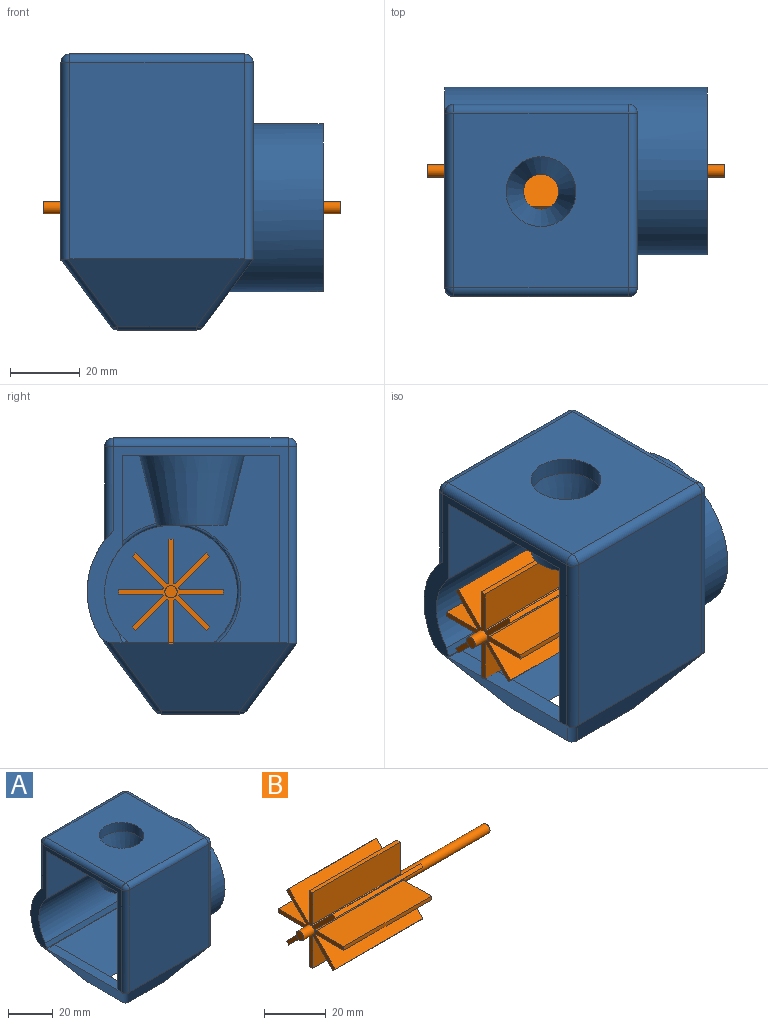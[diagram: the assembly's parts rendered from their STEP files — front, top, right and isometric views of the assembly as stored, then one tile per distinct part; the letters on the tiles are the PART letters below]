
ASSEMBLY  parts=2 mates=1
PART A: 60 faces, bbox 77.2x60.7x79.7 mm
  f0: cylinder r=19mm len=70mm, axis (-1,0,0), area 3704.2mm2, adj f1,f54,f55,f56,f57,f58,f59
  f1: plane 51.34x26.49mm, normal (0,-1,0), area 1308.1mm2, adj f0,f2,f53,f54,f58
  f2: plane 50x45mm, normal (0,0,-1), area 1543.1mm2, adj f1,f3,f52,f53,f54
  f3: plane 53.66x50mm, normal (0,1,0), area 2683.1mm2, adj f2,f4,f51,f53,f54
  f4: plane 45x5mm, normal (0,0,1), area 225mm2, adj f3,f5,f49,f50
  f5: plane 45x20.34mm, normal (0.8,0,0.59), area 758.1mm2, adj f4,f6,f48,f51
  f6: plane 22.48x22.48mm, normal (0,0,-1), area 280.1mm2, adj f5,f7,f9,f44,f45,f47,f48,f51
  f7: plane 45.1x20.58mm, normal (-0.8,0,0.59), area 653.9mm2, adj f6,f8,f48,f51,f53,f56,f57,f58
  f8: plane 0.44x0.42mm, normal (-1,0,0), area 0.1mm2, adj f7,f50,f55,f56
  f9: cylinder r=2.5mm len=22.48mm, axis (0,1,0), area 52.6mm2, adj f6,f10,f43,f49
  f10: sphere r=2.5mm, area 5.4mm2, adj f9,f11,f44
  f11: cylinder r=2.5mm len=19.59mm, axis (0.51,0.51,-0.69), area 84.3mm2, adj f10,f12,f42,f49
  f12: cylinder r=2.5mm len=56.22mm, axis (0,0,1), area 220.7mm2, adj f11,f13,f41,f42,f49,f54
  f13: sphere r=2.5mm, area 9.8mm2, adj f12,f14,f40
  f14: cylinder r=2.5mm len=50mm, axis (-1,0,0), area 196.3mm2, adj f13,f15,f39,f41
  f15: plane 50x50mm, normal (0,0,1), area 2185.8mm2, adj f14,f16,f19,f38,f40
  f16: cylinder r=10mm len=20mm, axis (0,0,-1), area 314.2mm2, adj f15,f17
  f17: cone r=10mm half-angle=14deg, axis (0,0,1), area 971.5mm2, adj f16,f18
  f18: plane 20x20mm, normal (0,0,-1), area 235.6mm2, adj f17,f52
  f19: cylinder r=2.5mm len=50mm, axis (1,0,0), area 196.3mm2, adj f15,f20,f36,f37
  f20: sphere r=2.5mm, area 9.8mm2, adj f19,f21,f40
  f21: cylinder r=2.5mm len=26.84mm, axis (0,0,1), area 100mm2, adj f20,f22,f36,f54
  f22: cylinder r=24mm len=75mm, axis (-1,0,0), area 4957.6mm2, adj f21,f23,f24,f26,f28,f32,f33,f34
  f23: cylinder r=24mm len=48mm, axis (-1,0,0), area 0mm2, adj f22,f35
  f24: plane 48x48mm, normal (1,0,0), area 1799.9mm2, adj f22,f25
  f25: cylinder r=1.75mm len=5mm, axis (-1,0,0), area 55mm2, adj f24,f59
  f26: cylinder r=2.5mm len=19.64mm, axis (-0.51,-0.51,-0.69), area 72.2mm2, adj f22,f27,f28,f35
  f27: sphere r=2.5mm, area 1.6mm2, adj f26,f45,f47
  f28: plane 46.83x19.35mm, normal (0.8,0,-0.59), area 583.5mm2, adj f22,f26,f29,f31,f32,f45
  f29: cylinder r=2.5mm len=19.59mm, axis (0.51,-0.51,0.69), area 84.3mm2, adj f28,f30,f31,f42
  f30: sphere r=2.5mm, area 4mm2, adj f29,f44,f45
  f31: cylinder r=2.5mm len=56.22mm, axis (0,0,-1), area 220.7mm2, adj f28,f29,f32,f39,f41,f42
  f32: plane 56.16x50mm, normal (1,0,0), area 1423.1mm2, adj f22,f28,f31,f33,f38
  f33: cylinder r=2.5mm len=26.84mm, axis (0,0,-1), area 100mm2, adj f22,f32,f36,f37
  f34: cylinder r=2.5mm len=21.73mm, axis (-0.51,0.51,0.69), area 89.3mm2, adj f22,f35,f43,f49,f54
  f35: plane 50.98x19.32mm, normal (0,0.8,-0.59), area 881.7mm2, adj f22,f23,f26,f34,f47
  f36: plane 50x26.84mm, normal (0,1,0), area 1341.9mm2, adj f19,f21,f22,f33
  f37: sphere r=2.5mm, area 6.2mm2, adj f19,f33,f38
  f38: cylinder r=2.5mm len=50mm, axis (0,-1,0), area 196.3mm2, adj f15,f32,f37,f39
  f39: sphere r=2.5mm, area 6.3mm2, adj f14,f31,f38
  f40: cylinder r=2.5mm len=50mm, axis (0,-1,0), area 196.3mm2, adj f13,f15,f20,f54
  f41: plane 56.16x50mm, normal (0,-1,0), area 2808.1mm2, adj f12,f14,f31,f42
  f42: plane 50.92x19.35mm, normal (0,-0.8,-0.59), area 881.7mm2, adj f11,f12,f29,f31,f41,f44
  f43: sphere r=2.5mm, area 5.4mm2, adj f9,f34,f47
  f44: cylinder r=2.5mm len=22.48mm, axis (1,0,0), area 52.6mm2, adj f6,f10,f30,f42
  f45: cylinder r=2.5mm len=22.48mm, axis (0,1,0), area 52.6mm2, adj f6,f27,f28,f30,f46
  f46: sphere r=2.5mm, area 0.4mm2, adj f45,f47
  f47: cylinder r=2.5mm len=22.48mm, axis (1,0,0), area 52.6mm2, adj f6,f27,f35,f43,f46
  f48: plane 45x20.34mm, normal (0,-0.8,0.59), area 758.1mm2, adj f5,f6,f7,f50
  f49: plane 50.96x19.35mm, normal (-0.8,0,-0.59), area 881.7mm2, adj f4,f9,f11,f12,f34,f54
  f50: plane 50x0.31mm, normal (0,-1,0), area 15.3mm2, adj f4,f8,f48,f54,f55
  f51: plane 45x20.34mm, normal (0,0.8,0.59), area 758.1mm2, adj f3,f5,f6,f7
  f52: cone r=15mm half-angle=14deg, axis (0,0,1), area 1619.1mm2, adj f2,f18
  f53: plane 53.66x45mm, normal (-1,0,0), area 1376mm2, adj f1,f2,f3,f7,f58
  f54: plane 58.17x56.83mm, normal (-1,0,0), area 480.4mm2, adj f0,f1,f2,f3,f12,f21,f22,f34
  f55: plane 51.46x3.01mm, normal (0,-0.94,0.33), area 135.8mm2, adj f0,f8,f50,f54,f56
  f56: torus R=20mm, axis (1,0,0), area 3.2mm2, adj f0,f7,f8,f55,f57
  f57: bspline ~26.48x5.21mm, area 29.1mm2, adj f0,f7,f56,f58
  f58: torus R=20mm, axis (1,0,0), area 97.7mm2, adj f0,f1,f7,f53,f57
  f59: plane 38x38mm, normal (-1,0,0), area 1124.5mm2, adj f0,f25
PART B: 38 faces, bbox 85x30x30 mm
  f0: cylinder r=15mm len=40mm, axis (-1,0,0), area 60mm2, adj f8,f9,f11,f32
  f1: cylinder r=15mm len=40mm, axis (-1,0,0), area 60mm2, adj f8,f9,f28,f31
  f2: cylinder r=15mm len=40mm, axis (-1,0,0), area 60mm2, adj f8,f9,f26,f29
  f3: cylinder r=15mm len=40mm, axis (-1,0,0), area 60mm2, adj f8,f9,f22,f25
  f4: cylinder r=15mm len=40mm, axis (-1,0,0), area 60mm2, adj f8,f9,f20,f23
  f5: cylinder r=15mm len=40mm, axis (-1,0,0), area 60mm2, adj f8,f9,f17,f19
  f6: cylinder r=15mm len=40mm, axis (-1,0,0), area 60mm2, adj f8,f9,f13,f16
  f7: cylinder r=15mm len=40mm, axis (-1,0,0), area 60mm2, adj f8,f9,f10,f14
  f8: plane 30x30mm, normal (-1,0,0), area 160.4mm2, adj f0,f1,f2,f3,f4,f5,f6,f7
  f9: plane 30x30mm, normal (1,0,0), area 160.4mm2, adj f0,f1,f2,f3,f4,f5,f6,f7
  f10: plane 40x12.6mm, normal (0,0,-1), area 503.9mm2, adj f7,f8,f9,f12
  f11: plane 40x8.91mm, normal (0,-0.71,0.71), area 503.9mm2, adj f0,f8,f9,f12
  f12: cylinder r=2.5mm len=40mm, axis (1,0,0), area 17.2mm2, adj f8,f9,f10,f11
  f13: plane 40x8.91mm, normal (0,-0.71,-0.71), area 503.8mm2, adj f6,f8,f9,f15
  f14: plane 40x12.6mm, normal (0,0,1), area 503.9mm2, adj f7,f8,f9,f15
  f15: cylinder r=2.5mm len=40mm, axis (1,0,0), area 18mm2, adj f8,f9,f13,f14
  f16: plane 40x8.91mm, normal (0,0.71,0.71), area 503.9mm2, adj f6,f8,f9,f18
  f17: plane 40x12.6mm, normal (0,-1,0), area 503.9mm2, adj f5,f8,f9,f18
  f18: cylinder r=2.5mm len=40mm, axis (1,0,0), area 17.2mm2, adj f8,f9,f16,f17
  f19: plane 40x12.6mm, normal (0,1,0), area 503.9mm2, adj f5,f8,f9,f21
  f20: plane 40x8.91mm, normal (0,-0.71,0.71), area 503.9mm2, adj f4,f8,f9,f21
  f21: cylinder r=2.5mm len=40mm, axis (1,0,0), area 17.2mm2, adj f8,f9,f19,f20
  f22: plane 40x12.6mm, normal (0,0,1), area 503.9mm2, adj f3,f8,f9,f24
  f23: plane 40x8.91mm, normal (0,0.71,-0.71), area 503.8mm2, adj f4,f8,f9,f24
  f24: cylinder r=2.5mm len=40mm, axis (1,0,0), area 18mm2, adj f8,f9,f22,f23
  f25: plane 40x12.6mm, normal (0,0,-1), area 503.9mm2, adj f3,f8,f9,f27
  f26: plane 40x8.91mm, normal (0,0.71,0.71), area 503.9mm2, adj f2,f8,f9,f27
  f27: cylinder r=2.5mm len=40mm, axis (1,0,0), area 17.2mm2, adj f8,f9,f25,f26
  f28: plane 40x12.6mm, normal (0,1,0), area 503.9mm2, adj f1,f8,f9,f30
  f29: plane 40x8.91mm, normal (0,-0.71,-0.71), area 503.8mm2, adj f2,f8,f9,f30
  f30: cylinder r=2.5mm len=40mm, axis (1,0,0), area 18mm2, adj f8,f9,f28,f29
  f31: plane 40x12.6mm, normal (0,-1,0), area 503.9mm2, adj f1,f8,f9,f33
  f32: plane 40x8.91mm, normal (0,0.71,-0.71), area 503.8mm2, adj f0,f8,f9,f33
  f33: cylinder r=2.5mm len=40mm, axis (1,0,0), area 18mm2, adj f8,f9,f31,f32
  f34: plane 3.5x3.5mm, normal (-1,0,0), area 9.6mm2, adj f35
  f35: cylinder r=1.75mm len=5mm, axis (1,0,0), area 55mm2, adj f8,f34
  f36: cylinder r=1.75mm len=40mm, axis (1,0,0), area 439.8mm2, adj f9,f37
  f37: plane 3.5x3.5mm, normal (1,0,0), area 9.6mm2, adj f36
PLACE A rot(axis=(-0.85,-0.48,-0.24),0deg) t=(-25.3,54.04,23.28)mm
PLACE B rot(axis=(-0.85,-0.48,-0.24),0deg) t=(-32.8,62.54,21.28)mm
MATE revolute B.f0 <-> A.f0  axis (1,0,0) through (7.2,62.54,21.28)mm
